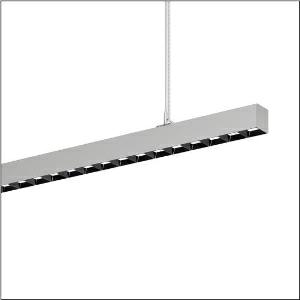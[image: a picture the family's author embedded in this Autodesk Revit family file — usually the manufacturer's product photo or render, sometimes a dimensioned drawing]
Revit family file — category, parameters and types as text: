
# Revit family: silica_r__21_51mx31tctds_9889
name_source: partatom
category: Lighting Fixtures
units: mm (PartAtom-declared; Revit-internal decimal feet)

## family parameters
Cut with Voids When Loaded = No
Host = Face
Light Source = No
Part Type = Normal
Room Calculation Point = No
Round Connector Dimension = Use Diameter
Shared = No

## types (1)
- --- (1 x LED, 15550 lm, 133.9 W, 6500K)
    Apparent Load = 134 VA
    CIE Flux Codes = 85 99 100 60 100
    Color Rendering = 80
    Color Temperature = 6500K
    Default Elevation = 1800 mm
    Description = Silica® 21, office luminaire, primary light control with darklight reflector, of PMMA, black, CAT 2 (L<= 3000cd/m²), light emission: direct/indirect distribution, primary light characteristic: symmetric, installation type: suspended mounting, LED, rated luminous flux: 15.550lm, luminous efficacy: 111lm/W, light colour: 8tw, colour temperature: 2700..6500K, control gear: ECG DALI, with terminal, 3+2-pole, max. 2.5mm², mains connection: 220..240V, AC, 50/60Hz, rated input power: 140.6W, luminaire housing, of aluminium, metallic grey (RAL 9006), length: 3.004mm, width: 53mm, height: 53mm, protection rating (complete): IP20, insulation class (complete): insulation class I (protective earthing), certification: CE, permissible operating ambient temperature: 0..+35°C, standard: EN 50419, packaging unit: 1 piece
    Height = 53 mm
    Lamp = 1 x LED
    Lamp Light Flux = 15550 lm
    Lamp Power = 133.9 W
    Lamp count = 1
    Length = 3004 mm
    Luminous efficacy = 116 lm/W
    Manufacturer = Siteco
    ModVariant = No
    Model = 51MX31TCTDS
    Mounting Place = Ceiling
    Mounting Type = Pendant
    Number of Poles = 1
    OnlyDefault = Yes
    Power Factor = 1
    Product Name = Silica® 21
    Product group = office luminaire | ceiling pendant
    ProductGroupID = 902
    Protection Class = Protection class I
    Protection Degree = IP 20
    RLX_Detail_Level = 1
    RLX_Emergency_Light_Flux = 0 lm
    RLX_Emergency_Type = 0
    RLX_Emergency_Type_DB = No
    RlxData = <blob elided: 61969 chars, md5=91677351>
    Socket = socket
    Standby Power = 0 W
    System Light Flux = 15550 lm
    System Power = 134 W
    Type Comments = individual setting
    Type Image = l_1297751.jpg
    URL = http://relux.com
    VarID = @adj_071185
    Voltage = 0 V
    Weight = 0.00 kg
    Width = 53 mm

## geometry (parser evidence)
native form markers: Blend x4, Sweep x13
no freeform markers — native parametric forms only
